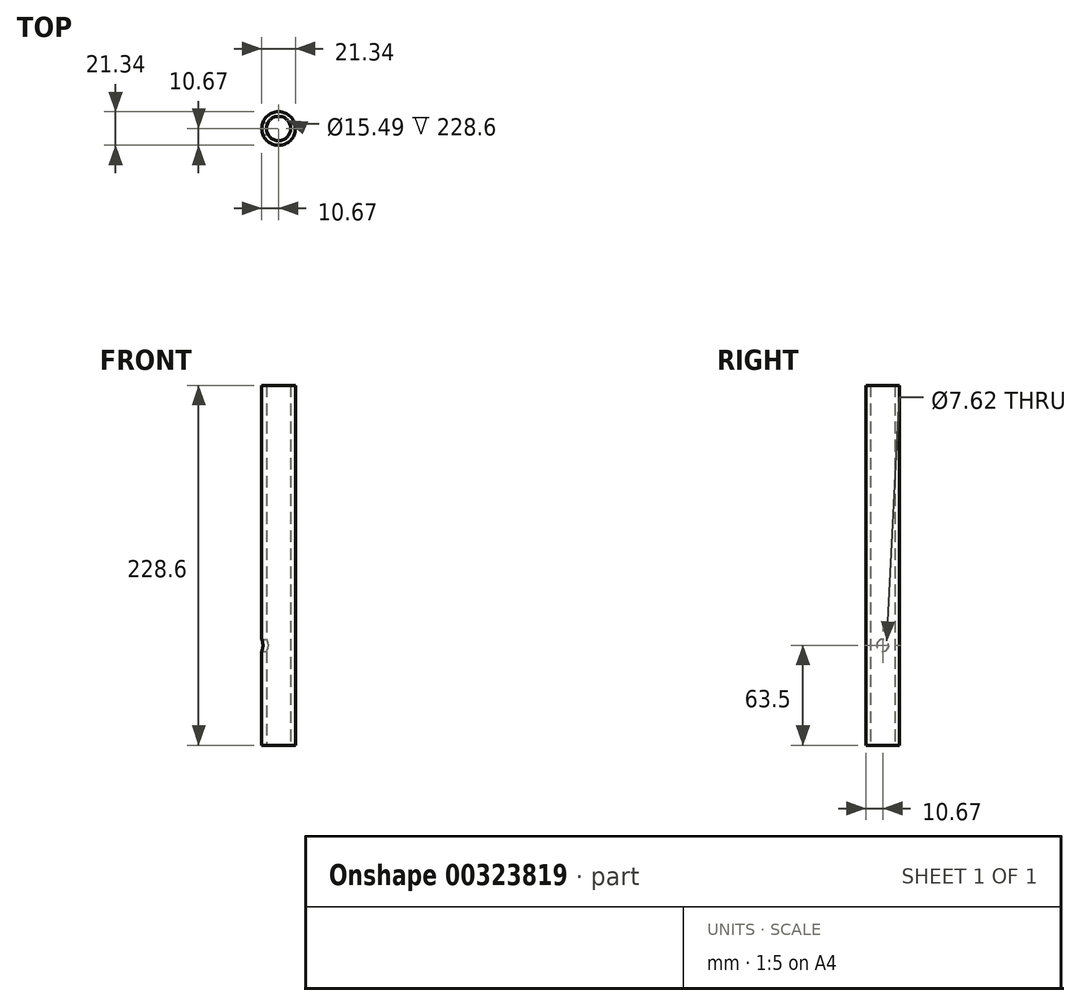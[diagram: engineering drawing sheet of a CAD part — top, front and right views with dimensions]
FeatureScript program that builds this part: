
annotation { "Feature Type Name" : "Feature", "Feature Type Description" : "" }
export const myFeature = defineFeature(function(context is Context, id is Id, definition is map)
    precondition{}
    {
        {
            var Q0;
            Q0=qCreatedBy(makeId("Top.planeOp"),FACE);
            var sketch = newSketch(context, id + "F0", { "sketchPlane" : qUnion([Q0])});
            skCircle(sketch, "E0", {"center": v(0, 0) * mm, "radius": 7.75 * mm});
            skCircle(sketch, "E1", {"center": v(0, 0) * mm, "radius": 10.67 * mm});
            skSolve(sketch);
        }
        {
            var Q0;
            Q0=makeQuery(id+"F0.imprint","IMPRINT",FACE,{"disambiguationData":[TD([[makeQuery(id+"F0.imprint","IMPRINT",EDGE,{"derivedFrom":sQuery(id+"F0.wireOp",EDGE,"E0")}),-1.0]])]});
            extrude(context, id + "F1", {"entities" : qUnion([Q0]), "depth" : 228.6 * mm});
        }
        {
            var Q0;
            Q0=qCreatedBy(makeId("Right.planeOp"),FACE);
            var sketch = newSketch(context, id + "F2", { "sketchPlane" : qUnion([Q0])});
            skCircle(sketch, "E2", {"center": v(0, 63.5) * mm, "radius": 3.81 * mm});
            skLineSegment(sketch, "E3", {"start": v(-10.67, 0) * mm, "end": v(-10.67, 228.6) * mm});
            skLineSegment(sketch, "E4", {"start": v(10.67, 228.6) * mm, "end": v(10.67, 0) * mm});
            skLineSegment(sketch, "E5.0", {"start": v(-10.67, 0) * mm, "end": v(10.67, 0) * mm});
            skLineSegment(sketch, "E6", {"start": v(0, 0) * mm, "end": v(0, -8.36) * mm, "construction": true});
            skPoint(sketch, "E6.endSnap0", {"position": v(0, 0) * mm});
            skSolve(sketch);
        }
        {
            var Q0;
            Q0=makeQuery(id+"F2.imprint","IMPRINT",FACE,{"disambiguationData":[TD([[makeQuery(id+"F2.imprint","IMPRINT",EDGE,{"derivedFrom":sQuery(id+"F2.wireOp",EDGE,"E2")}),1.0]])]});
            extrude(context, id + "F3", {"entities" : qUnion([Q0]), "operationType" : NewBodyOperationType.REMOVE, "oppositeDirection" : true, "depth" : 25.4 * mm});
        }
    });
